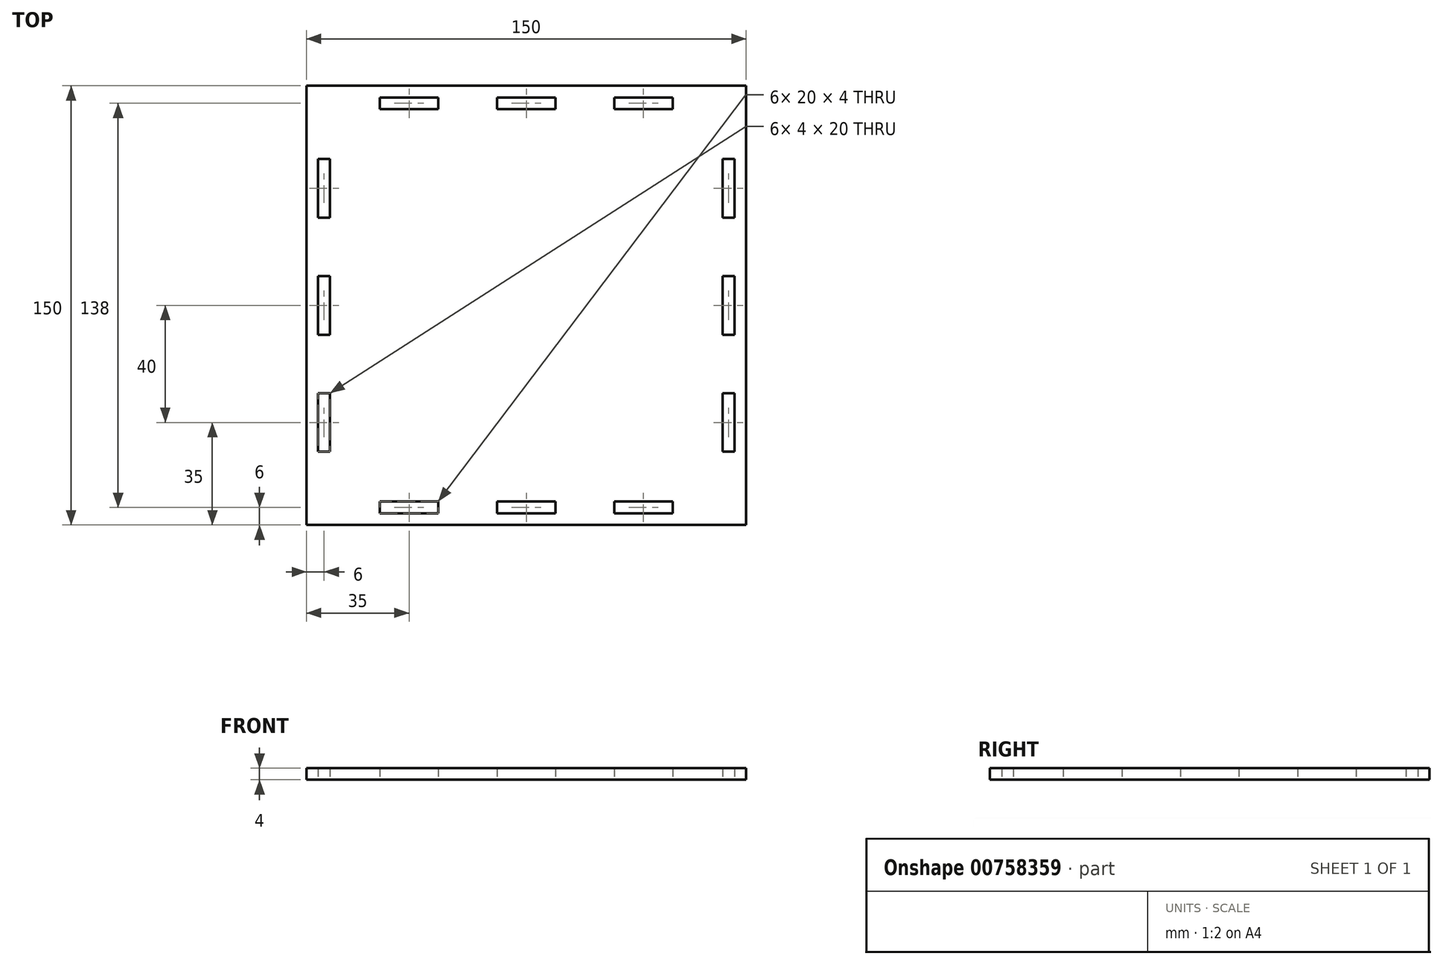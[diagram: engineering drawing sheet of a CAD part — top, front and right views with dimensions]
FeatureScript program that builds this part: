
annotation { "Feature Type Name" : "Feature", "Feature Type Description" : "" }
export const myFeature = defineFeature(function(context is Context, id is Id, definition is map)
    precondition{}
    {
        {
            var Q0;
            Q0=qCreatedBy(makeId("Top.planeOp"),FACE);
            var sketch = newSketch(context, id + "F0", { "sketchPlane" : qUnion([Q0])});
            skLineSegment(sketch, "E0.bottom", {"start": v(75, 75) * mm, "end": v(-75, 75) * mm});
            skLineSegment(sketch, "E0.top", {"start": v(75, -75) * mm, "end": v(-75, -75) * mm});
            skLineSegment(sketch, "E0.left", {"start": v(75, 75) * mm, "end": v(75, -75) * mm});
            skLineSegment(sketch, "E0.right", {"start": v(-75, 75) * mm, "end": v(-75, -75) * mm});
            skPoint(sketch, "E0.middle", {"position": v(0, 0) * mm});
            skLineSegment(sketch, "E1", {"start": v(0, 71) * mm, "end": v(10, 71) * mm});
            skLineSegment(sketch, "E2", {"start": v(10, 71) * mm, "end": v(10, 67) * mm});
            skLineSegment(sketch, "E3", {"start": v(10, 67) * mm, "end": v(0, 67) * mm});
            skLineSegment(sketch, "E4.MirrorCS", {"start": v(-10, 67) * mm, "end": v(0, 67) * mm});
            skLineSegment(sketch, "E5.MirrorCS", {"start": v(0, 71) * mm, "end": v(-10, 71) * mm});
            skLineSegment(sketch, "E6.MirrorCS", {"start": v(-10, 71) * mm, "end": v(-10, 67) * mm});
            skLineSegment(sketch, "E7.1.0.0", {"start": v(40, 71) * mm, "end": v(30, 71) * mm});
            skLineSegment(sketch, "E7.1.0.1", {"start": v(30, 67) * mm, "end": v(40, 67) * mm});
            skLineSegment(sketch, "E7.1.0.2", {"start": v(40, 71) * mm, "end": v(50, 71) * mm});
            skLineSegment(sketch, "E7.1.0.3", {"start": v(50, 67) * mm, "end": v(40, 67) * mm});
            skLineSegment(sketch, "E7.1.0.4", {"start": v(50, 71) * mm, "end": v(50, 67) * mm});
            skLineSegment(sketch, "E7.1.0.5", {"start": v(30, 71) * mm, "end": v(30, 67) * mm});
            skLineSegment(sketch, "E8.MirrorCS", {"start": v(-30, 67) * mm, "end": v(-40, 67) * mm});
            skLineSegment(sketch, "E9.MirrorCS", {"start": v(-30, 71) * mm, "end": v(-30, 67) * mm});
            skLineSegment(sketch, "E10.MirrorCS", {"start": v(-40, 71) * mm, "end": v(-30, 71) * mm});
            skLineSegment(sketch, "E11.MirrorCS", {"start": v(-50, 67) * mm, "end": v(-40, 67) * mm});
            skLineSegment(sketch, "E12.MirrorCS", {"start": v(-40, 71) * mm, "end": v(-50, 71) * mm});
            skLineSegment(sketch, "E13.MirrorCS", {"start": v(-50, 71) * mm, "end": v(-50, 67) * mm});
            skLineSegment(sketch, "E14.MirrorCS", {"start": v(-10, -67) * mm, "end": v(0, -67) * mm});
            skLineSegment(sketch, "E15.MirrorCS", {"start": v(10, -67) * mm, "end": v(0, -67) * mm});
            skLineSegment(sketch, "E16.MirrorCS", {"start": v(0, -71) * mm, "end": v(-10, -71) * mm});
            skLineSegment(sketch, "E17.MirrorCS", {"start": v(0, -71) * mm, "end": v(10, -71) * mm});
            skLineSegment(sketch, "E18.MirrorCS", {"start": v(-40, -71) * mm, "end": v(-30, -71) * mm});
            skLineSegment(sketch, "E19.MirrorCS", {"start": v(-40, -71) * mm, "end": v(-50, -71) * mm});
            skLineSegment(sketch, "E20.MirrorCS", {"start": v(-50, -67) * mm, "end": v(-40, -67) * mm});
            skLineSegment(sketch, "E21.MirrorCS", {"start": v(-30, -67) * mm, "end": v(-40, -67) * mm});
            skLineSegment(sketch, "E22.MirrorCS", {"start": v(40, -71) * mm, "end": v(30, -71) * mm});
            skLineSegment(sketch, "E23.MirrorCS", {"start": v(40, -71) * mm, "end": v(50, -71) * mm});
            skLineSegment(sketch, "E24.MirrorCS", {"start": v(50, -67) * mm, "end": v(40, -67) * mm});
            skLineSegment(sketch, "E25.MirrorCS", {"start": v(30, -67) * mm, "end": v(40, -67) * mm});
            skLineSegment(sketch, "E26.MirrorCS", {"start": v(50, -71) * mm, "end": v(50, -67) * mm});
            skLineSegment(sketch, "E27.MirrorCS", {"start": v(30, -71) * mm, "end": v(30, -67) * mm});
            skLineSegment(sketch, "E28.MirrorCS", {"start": v(10, -71) * mm, "end": v(10, -67) * mm});
            skLineSegment(sketch, "E29.MirrorCS", {"start": v(-10, -71) * mm, "end": v(-10, -67) * mm});
            skLineSegment(sketch, "E30.MirrorCS", {"start": v(-50, -71) * mm, "end": v(-50, -67) * mm});
            skLineSegment(sketch, "E31.MirrorCS", {"start": v(-30, -71) * mm, "end": v(-30, -67) * mm});
            skLineSegment(sketch, "E32", {"start": v(-71, 0) * mm, "end": v(-71, 10) * mm});
            skLineSegment(sketch, "E33", {"start": v(-71, 10) * mm, "end": v(-67, 10) * mm});
            skLineSegment(sketch, "E34", {"start": v(-67, 10) * mm, "end": v(-67, -10) * mm});
            skLineSegment(sketch, "E35", {"start": v(-67, -10) * mm, "end": v(-71, -10) * mm});
            skLineSegment(sketch, "E36", {"start": v(-71, -10) * mm, "end": v(-71, 0) * mm});
            skLineSegment(sketch, "E37.0.1.0", {"start": v(-67, 50) * mm, "end": v(-67, 30) * mm});
            skLineSegment(sketch, "E37.0.1.1", {"start": v(-71, 40) * mm, "end": v(-71, 50) * mm});
            skLineSegment(sketch, "E37.0.1.2", {"start": v(-71, 30) * mm, "end": v(-71, 40) * mm});
            skLineSegment(sketch, "E37.0.1.3", {"start": v(-67, 30) * mm, "end": v(-71, 30) * mm});
            skLineSegment(sketch, "E37.0.1.4", {"start": v(-71, 50) * mm, "end": v(-67, 50) * mm});
            skLineSegment(sketch, "E37.1.1.0", {"start": v(-67, 50) * mm, "end": v(-67, 30) * mm});
            skLineSegment(sketch, "E37.1.1.1", {"start": v(-71, 40) * mm, "end": v(-71, 50) * mm});
            skLineSegment(sketch, "E37.1.1.2", {"start": v(-71, 30) * mm, "end": v(-71, 40) * mm});
            skLineSegment(sketch, "E37.1.1.3", {"start": v(-67, 30) * mm, "end": v(-71, 30) * mm});
            skLineSegment(sketch, "E37.1.1.4", {"start": v(-71, 50) * mm, "end": v(-67, 50) * mm});
            skLineSegment(sketch, "E37.2.0.0", {"start": v(-67, 0) * mm, "end": v(-67, 0) * mm});
            skLineSegment(sketch, "E37.2.0.2", {"start": v(-71, 0) * mm, "end": v(-71, -10) * mm});
            skLineSegment(sketch, "E37.2.0.3", {"start": v(-67, 0) * mm, "end": v(-71, 0) * mm});
            skLineSegment(sketch, "E37.2.0.4", {"start": v(-71, 0) * mm, "end": v(-67, 0) * mm});
            skLineSegment(sketch, "E37.2.1.0", {"start": v(-67, 50) * mm, "end": v(-67, 30) * mm});
            skLineSegment(sketch, "E37.2.1.1", {"start": v(-71, 40) * mm, "end": v(-71, 50) * mm});
            skLineSegment(sketch, "E37.2.1.2", {"start": v(-71, 30) * mm, "end": v(-71, 40) * mm});
            skLineSegment(sketch, "E37.2.1.3", {"start": v(-67, 30) * mm, "end": v(-71, 30) * mm});
            skLineSegment(sketch, "E37.2.1.4", {"start": v(-71, 50) * mm, "end": v(-67, 50) * mm});
            skLineSegment(sketch, "E37.direction1", {"start": v(-67, -10) * mm, "end": v(-67, -10) * mm});
            skLineSegment(sketch, "E38.MirrorCS", {"start": v(-67, -30) * mm, "end": v(-71, -30) * mm});
            skLineSegment(sketch, "E39.MirrorCS", {"start": v(-71, -30) * mm, "end": v(-71, -40) * mm});
            skLineSegment(sketch, "E40.MirrorCS", {"start": v(-67, -50) * mm, "end": v(-67, -30) * mm});
            skLineSegment(sketch, "E41.MirrorCS", {"start": v(-71, -40) * mm, "end": v(-71, -50) * mm});
            skLineSegment(sketch, "E42.MirrorCS", {"start": v(-71, -50) * mm, "end": v(-67, -50) * mm});
            skLineSegment(sketch, "E43.MirrorCS", {"start": v(67, -50) * mm, "end": v(67, -30) * mm});
            skLineSegment(sketch, "E44.MirrorCS", {"start": v(71, -30) * mm, "end": v(71, -40) * mm});
            skLineSegment(sketch, "E45.MirrorCS", {"start": v(71, -40) * mm, "end": v(71, -50) * mm});
            skLineSegment(sketch, "E46.MirrorCS", {"start": v(71, -50) * mm, "end": v(67, -50) * mm});
            skLineSegment(sketch, "E47.MirrorCS", {"start": v(67, -30) * mm, "end": v(71, -30) * mm});
            skLineSegment(sketch, "E48.MirrorCS", {"start": v(71, -10) * mm, "end": v(71, 0) * mm});
            skLineSegment(sketch, "E49.MirrorCS", {"start": v(71, 0) * mm, "end": v(71, 10) * mm});
            skLineSegment(sketch, "E50.MirrorCS", {"start": v(67, 10) * mm, "end": v(67, -10) * mm});
            skLineSegment(sketch, "E51.MirrorCS", {"start": v(71, 10) * mm, "end": v(67, 10) * mm});
            skLineSegment(sketch, "E52.MirrorCS", {"start": v(67, 30) * mm, "end": v(71, 30) * mm});
            skLineSegment(sketch, "E53.MirrorCS", {"start": v(71, 30) * mm, "end": v(71, 40) * mm});
            skLineSegment(sketch, "E54.MirrorCS", {"start": v(71, 40) * mm, "end": v(71, 50) * mm});
            skLineSegment(sketch, "E55.MirrorCS", {"start": v(71, 50) * mm, "end": v(67, 50) * mm});
            skLineSegment(sketch, "E56.MirrorCS", {"start": v(67, 50) * mm, "end": v(67, 30) * mm});
            skLineSegment(sketch, "E57", {"start": v(67, -10) * mm, "end": v(71, -10) * mm});
            skSolve(sketch);
        }
        {
            var Q0;
            Q0=makeQuery(id+"F0.imprint","IMPRINT",FACE,{"disambiguationData":[TD([[makeQuery(id+"F0.imprint","IMPRINT",EDGE,{"derivedFrom":sQuery(id+"F0.wireOp",EDGE,"E0.bottom")}),1.0]])]});
            extrude(context, id + "F1", {"entities" : qUnion([Q0]), "depth" : 4 * mm});
        }
    });
